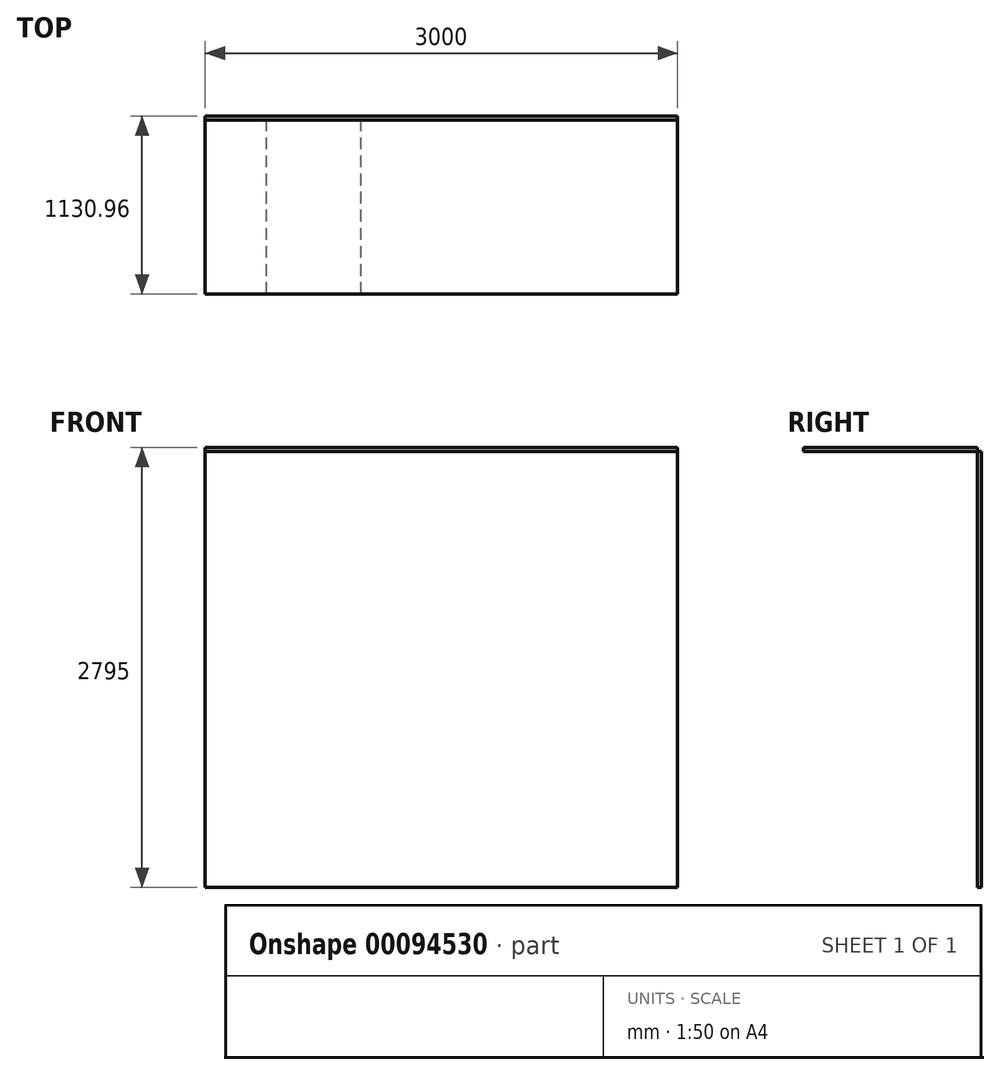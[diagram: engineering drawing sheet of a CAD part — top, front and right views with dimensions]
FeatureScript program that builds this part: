
annotation { "Feature Type Name" : "Feature", "Feature Type Description" : "" }
export const myFeature = defineFeature(function(context is Context, id is Id, definition is map)
    precondition{}
    {
        {
            var Q0;
            Q0=qCreatedBy(makeId("Front.planeOp"),FACE);
            var sketch = newSketch(context, id + "F0", { "sketchPlane" : qUnion([Q0])});
            skLineSegment(sketch, "E0.bottom", {"start": v(1500, 1385) * mm, "end": v(-1500, 1385) * mm});
            skLineSegment(sketch, "E0.top", {"start": v(1500, -1385) * mm, "end": v(-1500, -1385) * mm});
            skLineSegment(sketch, "E0.left", {"start": v(1500, 1385) * mm, "end": v(1500, -1385) * mm});
            skLineSegment(sketch, "E0.right", {"start": v(-1500, 1385) * mm, "end": v(-1500, -1385) * mm});
            skPoint(sketch, "E0.middle", {"position": v(0, 0) * mm});
            skSolve(sketch);
        }
        {
            var Q0;
            Q0=makeQuery(id+"F0.imprint","IMPRINT",FACE,{"disambiguationData":[TD([[makeQuery(id+"F0.imprint","IMPRINT",EDGE,{"derivedFrom":sQuery(id+"F0.wireOp",EDGE,"E0.bottom")}),1.0]])]});
            extrude(context, id + "F1", {"entities" : qUnion([Q0]), "oppositeDirection" : true, "depth" : 25 * mm});
        }
        {
            var Q0;
            Q0=makeQuery(id+"F1.opExtrude","SWEPT_FACE",FACE,{"disambiguationData":[OSD([sQuery(id+"F0.wireOp",EDGE,"E0.bottom")])]});
            var sketch = newSketch(context, id + "F2", { "sketchPlane" : qUnion([Q0])});
            skLineSegment(sketch, "E1.bottom", {"start": v(1500, 0) * mm, "end": v(-1500, 0) * mm});
            skLineSegment(sketch, "E1.top", {"start": v(1500, -1105.96) * mm, "end": v(-1500, -1105.96) * mm});
            skLineSegment(sketch, "E1.left", {"start": v(1500, 0) * mm, "end": v(1500, -1105.96) * mm});
            skLineSegment(sketch, "E1.right", {"start": v(-1500, 0) * mm, "end": v(-1500, -1105.96) * mm});
            skLineSegment(sketch, "E2", {"start": v(-1110.24, -1105.96) * mm, "end": v(-1110.24, 0) * mm});
            skLineSegment(sketch, "E3.0", {"start": v(-510.24, -1105.96) * mm, "end": v(-510.24, 0) * mm});
            skSolve(sketch);
        }
        {
            var Q0;
            Q0 = qSketchRegion(id + "F2", true);
            extrude(context, id + "F3", {"entities" : qUnion([Q0]), "depth" : 25 * mm});
        }
        {
            var Q0;
            {var subQ0=sQuery(id+"F2.wireOp",EDGE,"E2");Q0=makeQuery(id+"F2.imprint","IMPRINT",FACE,{"disambiguationData":[TD([[makeQuery(id+"F2.imprint","IMPRINT",EDGE,{"derivedFrom":subQ0}),-1.0]])]});}
            extrude(context, id + "F4", {"entities" : qUnion([Q0]), "operationType" : NewBodyOperationType.REMOVE, "depth" : 1 * mm});
        }
    });
